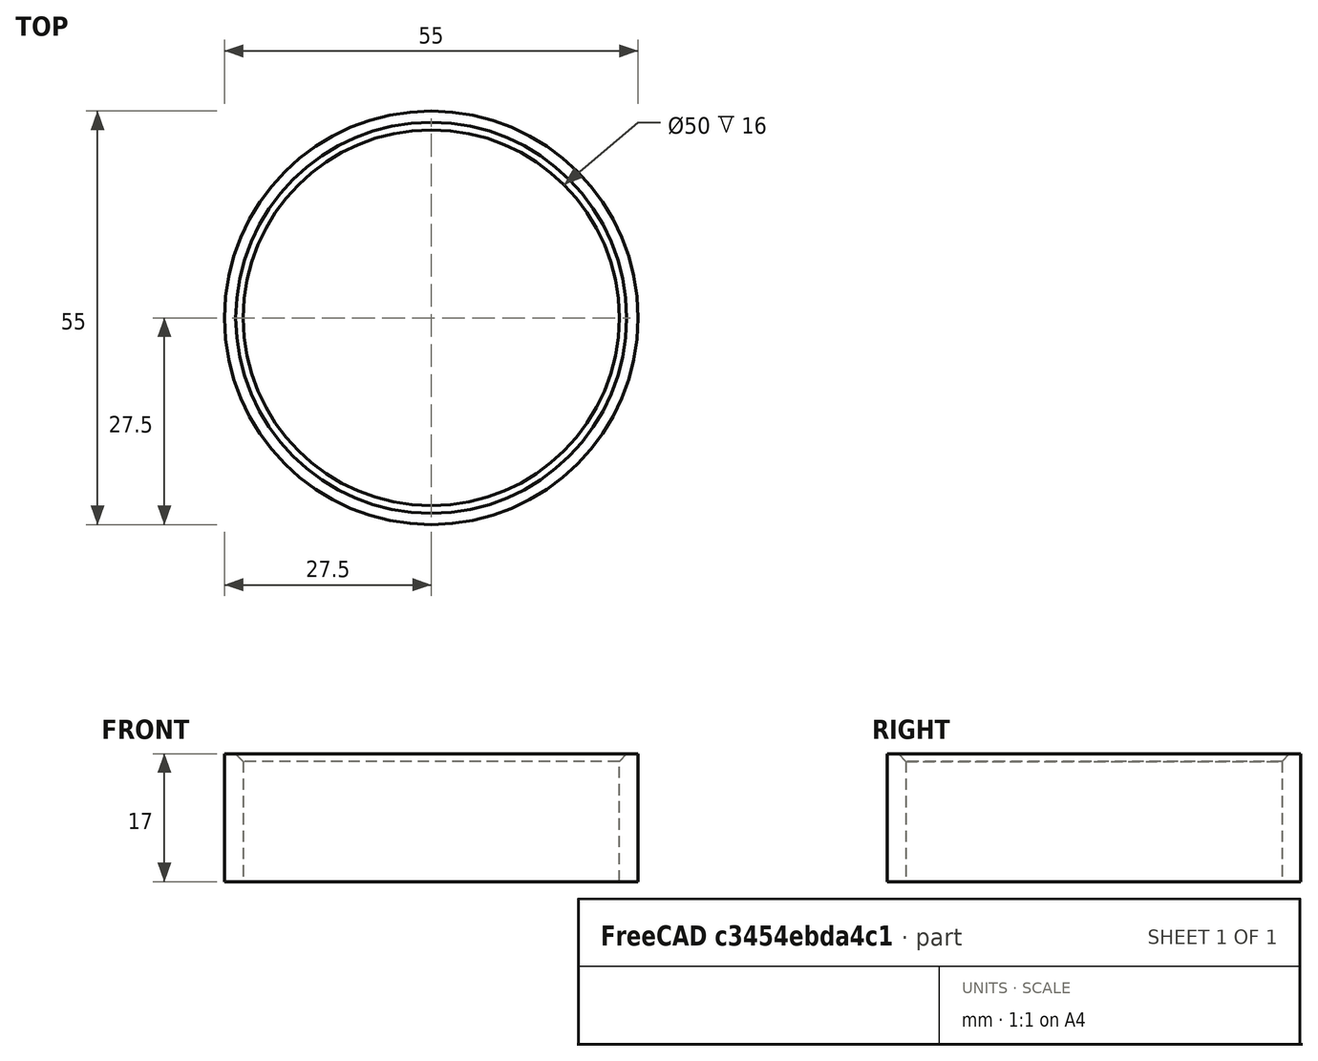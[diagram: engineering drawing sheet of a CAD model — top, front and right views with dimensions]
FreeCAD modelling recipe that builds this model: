
FCSTD DOCUMENT  (FreeCAD 0.19R24276 (Git))
Label: Stopper_from_Part_16_as3
License: All rights reserved
LicenseURL: http://en.wikipedia.org/wiki/All_rights_reserved
objects: Sketcher::SketchObject×1, PartDesign::Pad×1, PartDesign::Chamfer×1, PartDesign::Body×1
note: 6 computed .brp shape members not serialized (recipe doc carries the construction recipe); baked Part::Feature solids carry a one-line shape summary decoded from their .brp

FEATURE [Sketcher::SketchObject] Sketch  label="Sketch_d50_d55"
  FullyConstrained = true
  MapMode = 5
  Support = -> [XY_Plane]
  sketch-geometry (2):
    g0: Circle CenterX=0 CenterY=0 CenterZ=0 NormalX=0 NormalY=0 NormalZ=1 AngleXU=0 Radius=25
    g1: Circle CenterX=0 CenterY=0 CenterZ=0 NormalX=0 NormalY=0 NormalZ=1 AngleXU=0 Radius=27.5
  constraints (4):
    c: Coincident(g0,g-1)
    c: Coincident(g1,g0)
    c: Diameter(g0) = 50
    c: Diameter(g1) = 55
FEATURE [PartDesign::Pad] Pad  label="Pad_h17"
  Direction = (1,1,1)
  Length = 17
  Length2 = 100
  Profile = -> Sketch
  Type = 0
FEATURE [PartDesign::Chamfer] Chamfer
  Angle = 45
  Base = -> Pad [Edge6]
  BaseFeature = -> Pad
  ChamferType = 0
  FlipDirection = false
  Size = 1
  Size2 = 1
  SupportTransform = false
FEATURE [PartDesign::Body] Body
  Group = -> [Sketch,Pad,Chamfer]
  Origin = -> Origin
  Tip = -> Chamfer
